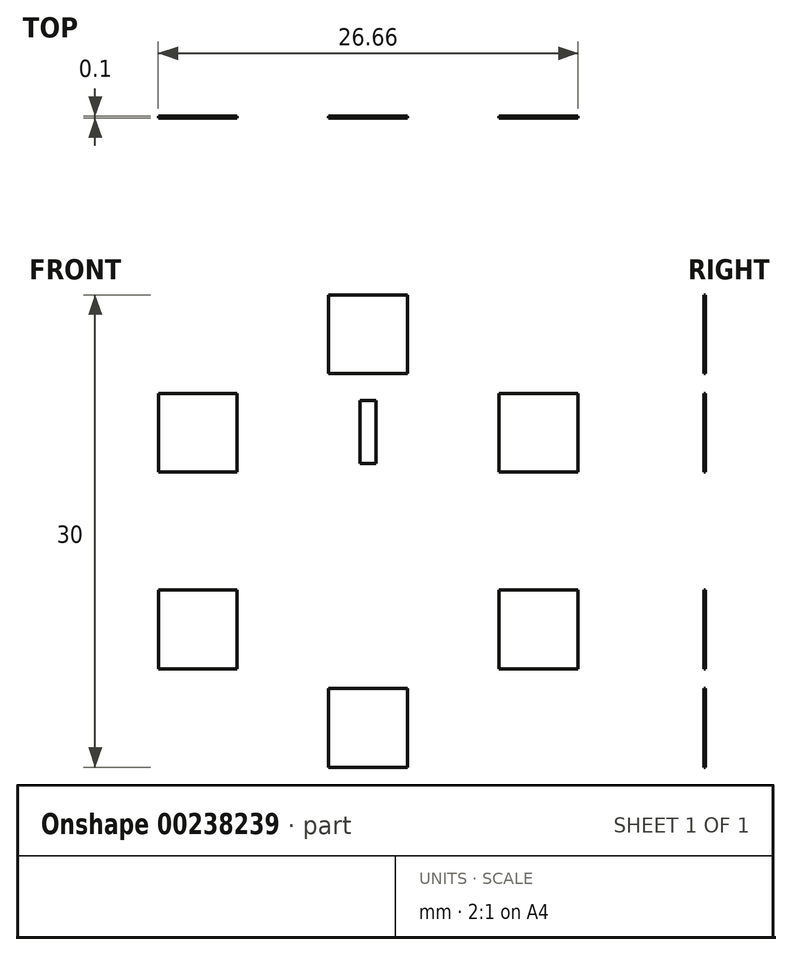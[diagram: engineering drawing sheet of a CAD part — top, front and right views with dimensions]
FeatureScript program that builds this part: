
annotation { "Feature Type Name" : "Feature", "Feature Type Description" : "" }
export const myFeature = defineFeature(function(context is Context, id is Id, definition is map)
    precondition{}
    {
        {
            var Q0;
            Q0=qCreatedBy(makeId("Front.planeOp"),FACE);
            var sketch = newSketch(context, id + "F0", { "sketchPlane" : qUnion([Q0])});
            skCircle(sketch, "E0", {"center": v(0, 0) * mm, "radius": 25.4 * mm, "construction": true});
            skCircle(sketch, "E1.cCircle", {"center": v(0, 0) * mm, "radius": 12.5 * mm, "construction": true});
            skLineSegment(sketch, "E1.0", {"start": v(0, 12.5) * mm, "end": v(10.83, 6.25) * mm, "construction": true});
            skLineSegment(sketch, "E1.1", {"start": v(10.83, 6.25) * mm, "end": v(10.83, -6.25) * mm, "construction": true});
            skLineSegment(sketch, "E1.2", {"start": v(10.83, -6.25) * mm, "end": v(0, -12.5) * mm, "construction": true});
            skLineSegment(sketch, "E1.3", {"start": v(0, -12.5) * mm, "end": v(-10.83, -6.25) * mm, "construction": true});
            skLineSegment(sketch, "E1.4", {"start": v(-10.83, -6.25) * mm, "end": v(-10.83, 6.25) * mm, "construction": true});
            skLineSegment(sketch, "E1.5", {"start": v(-10.83, 6.25) * mm, "end": v(0, 12.5) * mm, "construction": true});
            skLineSegment(sketch, "E2.bottom", {"start": v(2.5, 15) * mm, "end": v(-2.5, 15) * mm});
            skLineSegment(sketch, "E2.top", {"start": v(2.5, 10) * mm, "end": v(-2.5, 10) * mm});
            skLineSegment(sketch, "E2.left", {"start": v(2.5, 15) * mm, "end": v(2.5, 10) * mm});
            skLineSegment(sketch, "E2.right", {"start": v(-2.5, 15) * mm, "end": v(-2.5, 10) * mm});
            skPoint(sketch, "E2.middle", {"position": v(0, 12.5) * mm});
            skLineSegment(sketch, "E3.bottom", {"start": v(13.33, 8.75) * mm, "end": v(8.33, 8.75) * mm});
            skLineSegment(sketch, "E3.top", {"start": v(13.33, 3.75) * mm, "end": v(8.33, 3.75) * mm});
            skLineSegment(sketch, "E3.left", {"start": v(13.33, 8.75) * mm, "end": v(13.33, 3.75) * mm});
            skLineSegment(sketch, "E3.right", {"start": v(8.33, 8.75) * mm, "end": v(8.33, 3.75) * mm});
            skPoint(sketch, "E3.middle", {"position": v(10.83, 6.25) * mm});
            skLineSegment(sketch, "E4.bottom", {"start": v(13.33, -3.75) * mm, "end": v(8.33, -3.75) * mm});
            skLineSegment(sketch, "E4.top", {"start": v(13.33, -8.75) * mm, "end": v(8.33, -8.75) * mm});
            skLineSegment(sketch, "E4.left", {"start": v(13.33, -3.75) * mm, "end": v(13.33, -8.75) * mm});
            skLineSegment(sketch, "E4.right", {"start": v(8.33, -3.75) * mm, "end": v(8.33, -8.75) * mm});
            skPoint(sketch, "E4.middle", {"position": v(10.83, -6.25) * mm});
            skLineSegment(sketch, "E5.bottom", {"start": v(2.5, -15) * mm, "end": v(-2.5, -15) * mm});
            skLineSegment(sketch, "E5.top", {"start": v(2.5, -10) * mm, "end": v(-2.5, -10) * mm});
            skLineSegment(sketch, "E5.left", {"start": v(2.5, -15) * mm, "end": v(2.5, -10) * mm});
            skLineSegment(sketch, "E5.right", {"start": v(-2.5, -15) * mm, "end": v(-2.5, -10) * mm});
            skPoint(sketch, "E5.middle", {"position": v(0, -12.5) * mm});
            skLineSegment(sketch, "E6.bottom", {"start": v(-8.33, -3.75) * mm, "end": v(-13.33, -3.75) * mm});
            skLineSegment(sketch, "E6.top", {"start": v(-8.33, -8.75) * mm, "end": v(-13.33, -8.75) * mm});
            skLineSegment(sketch, "E6.left", {"start": v(-8.33, -3.75) * mm, "end": v(-8.33, -8.75) * mm});
            skLineSegment(sketch, "E6.right", {"start": v(-13.33, -3.75) * mm, "end": v(-13.33, -8.75) * mm});
            skPoint(sketch, "E6.middle", {"position": v(-10.83, -6.25) * mm});
            skLineSegment(sketch, "E7.bottom", {"start": v(-8.33, 3.75) * mm, "end": v(-13.33, 3.75) * mm});
            skLineSegment(sketch, "E7.top", {"start": v(-8.33, 8.75) * mm, "end": v(-13.33, 8.75) * mm});
            skLineSegment(sketch, "E7.left", {"start": v(-8.33, 3.75) * mm, "end": v(-8.33, 8.75) * mm});
            skLineSegment(sketch, "E7.right", {"start": v(-13.33, 3.75) * mm, "end": v(-13.33, 8.75) * mm});
            skPoint(sketch, "E7.middle", {"position": v(-10.83, 6.25) * mm});
            skLineSegment(sketch, "E8.bottom", {"start": v(0.5, 4.3) * mm, "end": v(-0.5, 4.3) * mm});
            skLineSegment(sketch, "E8.top", {"start": v(0.5, 8.3) * mm, "end": v(-0.5, 8.3) * mm});
            skLineSegment(sketch, "E8.left", {"start": v(0.5, 4.3) * mm, "end": v(0.5, 8.3) * mm});
            skLineSegment(sketch, "E8.right", {"start": v(-0.5, 4.3) * mm, "end": v(-0.5, 8.3) * mm});
            skPoint(sketch, "E8.middle", {"position": v(0, 6.3) * mm});
            skSolve(sketch);
        }
        {
            var Q0;
            Q0=qSketchRegion(id+"F0",true);
            extrude(context, id + "F1", {"entities" : qUnion([Q0]), "depth" : .1 * mm});
        }
    });
